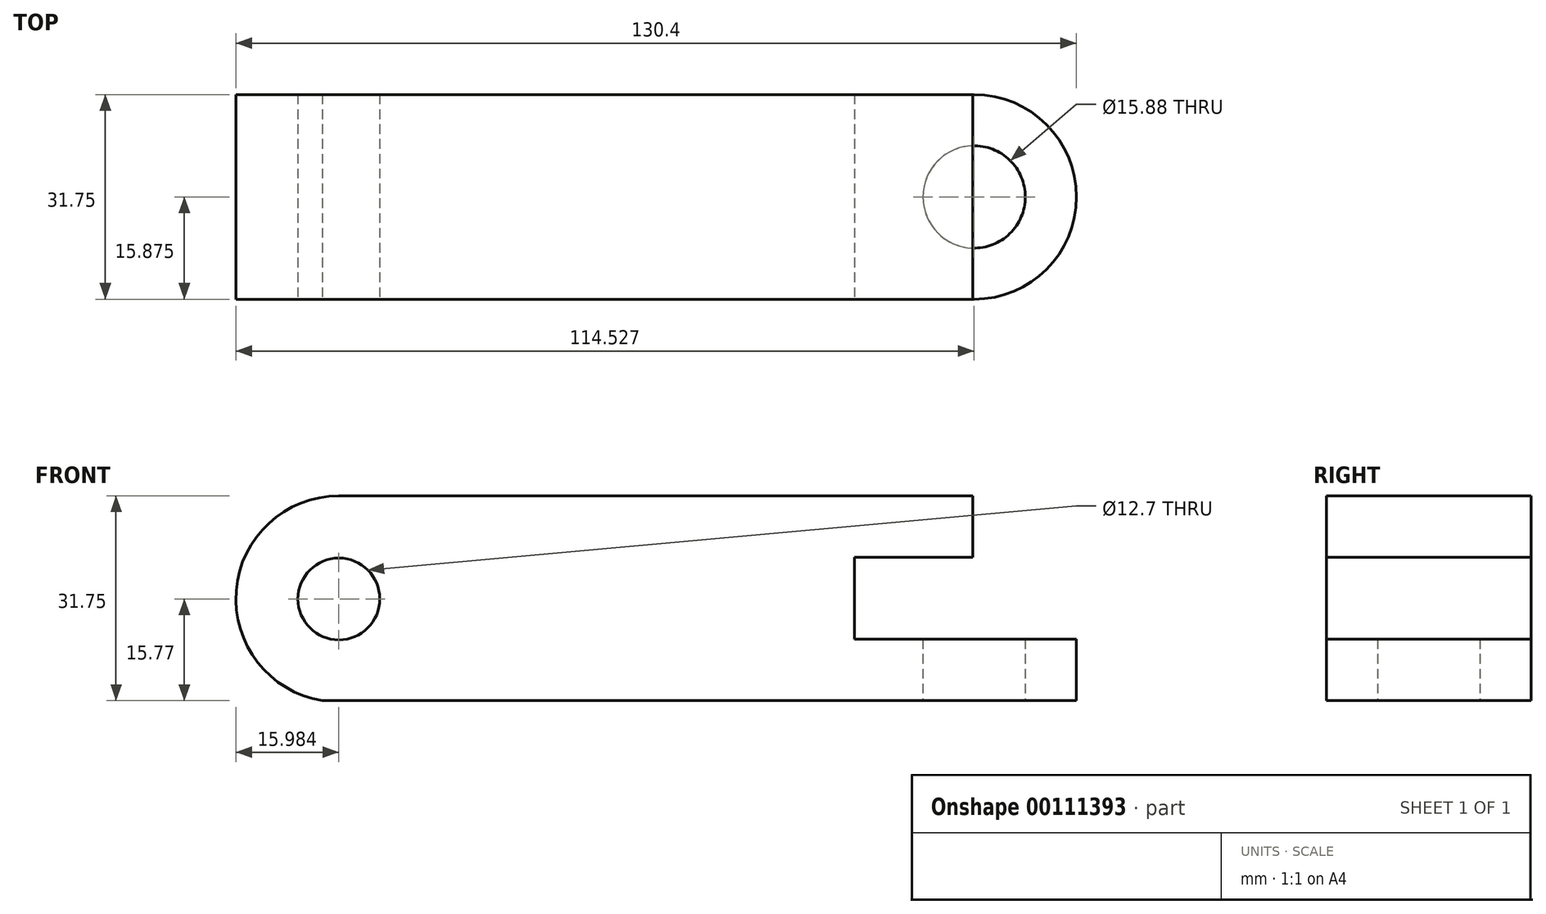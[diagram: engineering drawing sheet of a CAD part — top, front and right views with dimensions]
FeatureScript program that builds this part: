
annotation { "Feature Type Name" : "Feature", "Feature Type Description" : "" }
export const myFeature = defineFeature(function(context is Context, id is Id, definition is map)
    precondition{}
    {
        {
            var Q0;
            Q0=qCreatedBy(makeId("Front.planeOp"),FACE);
            var sketch = newSketch(context, id + "F0", { "sketchPlane" : qUnion([Q0])});
            skLineSegment(sketch, "E0", {"start": v(-48.21, 0) * mm, "end": v(52.92, 0) * mm});
            skLineSegment(sketch, "E1", {"start": v(52.92, 0) * mm, "end": v(52.92, 9.53) * mm});
            skLineSegment(sketch, "E2", {"start": v(52.92, 9.53) * mm, "end": v(34.34, 9.53) * mm});
            skLineSegment(sketch, "E3", {"start": v(34.34, 9.53) * mm, "end": v(34.34, 22.23) * mm});
            skLineSegment(sketch, "E4", {"start": v(34.34, 22.23) * mm, "end": v(52.68, 22.23) * mm});
            skLineSegment(sketch, "E5", {"start": v(52.68, 22.23) * mm, "end": v(52.68, 31.75) * mm});
            skLineSegment(sketch, "E6", {"start": v(52.68, 31.75) * mm, "end": v(-45.63, 31.75) * mm});
            skArc(sketch, "E7", {"start": v(-45.63, 31.75) * mm, "mid": v(-61.55, 17.07) * mm, "end": v(-48.21, 0) * mm});
            skCircle(sketch, "E8", {"center": v(-45.63, 15.77) * mm, "radius": 6.35 * mm});
            skSolve(sketch);
        }
        {
            var Q0;
            Q0 = qSketchRegion(id + "F0", true);
            extrude(context, id + "F1", {"entities" : qUnion([Q0]), "oppositeDirection" : true, "depth" : 31.75 * mm});
        }
        {
            var Q0;
            Q0=qCreatedBy(makeId("Top.planeOp"),FACE);
            var sketch = newSketch(context, id + "F2", { "sketchPlane" : qUnion([Q0])});
            skArc(sketch, "E9", {"start": v(52.92, 0) * mm, "mid": v(68.8, 15.88) * mm, "end": v(52.92, 31.75) * mm});
            skCircle(sketch, "E10", {"center": v(52.92, 15.88) * mm, "radius": 7.94 * mm});
            skCircle(sketch, "E11", {"center": v(52.92, 15.88) * mm, "radius": 15.88 * mm});
            skSolve(sketch);
        }
        {
            var Q0;
            Q0 = qSketchRegion(id + "F2", true);
            var Q1;
            Q1=makeQuery(id+"F1.opExtrude","SWEPT_FACE",FACE,{"disambiguationData":[OSD([sQuery(id+"F0.wireOp",EDGE,"E2")])]});
            extrude(context, id + "F3", {"entities" : qUnion([Q0]), "operationType" : NewBodyOperationType.ADD, "endBound" : BoundingType.UP_TO_SURFACE, "endBoundEntityFace" : qUnion([Q1]), "depth" : 12.66 * mm});
        }
        {
            var Q0;
            Q0=makeQuery(id+"F2.imprint","IMPRINT",FACE,{"disambiguationData":[TD([[makeQuery(id+"F2.imprint","IMPRINT",EDGE,{"derivedFrom":sQuery(id+"F2.wireOp",EDGE,"E10")}),1.0]])]});
            var Q1;
            {var subQ0=sQuery(id+"F0.wireOp",EDGE,"E2");Q1=makeQuery(id+"F3.boolean.opBoolean","MERGE",FACE,{"derivedFrom":[makeQuery(id+"F1.opExtrude","SWEPT_FACE",FACE,{"disambiguationData":[OSD([subQ0])]}),makeQuery(id+"F3.opExtrude","CAP_FACE",FACE,{"disambiguationData":[OSD([subQ0])],"isStart":false})]});}
            extrude(context, id + "F4", {"entities" : qUnion([Q0]), "operationType" : NewBodyOperationType.REMOVE, "endBound" : BoundingType.UP_TO_SURFACE, "endBoundEntityFace" : qUnion([Q1]), "depth" : 7.63 * mm});
        }
    });
